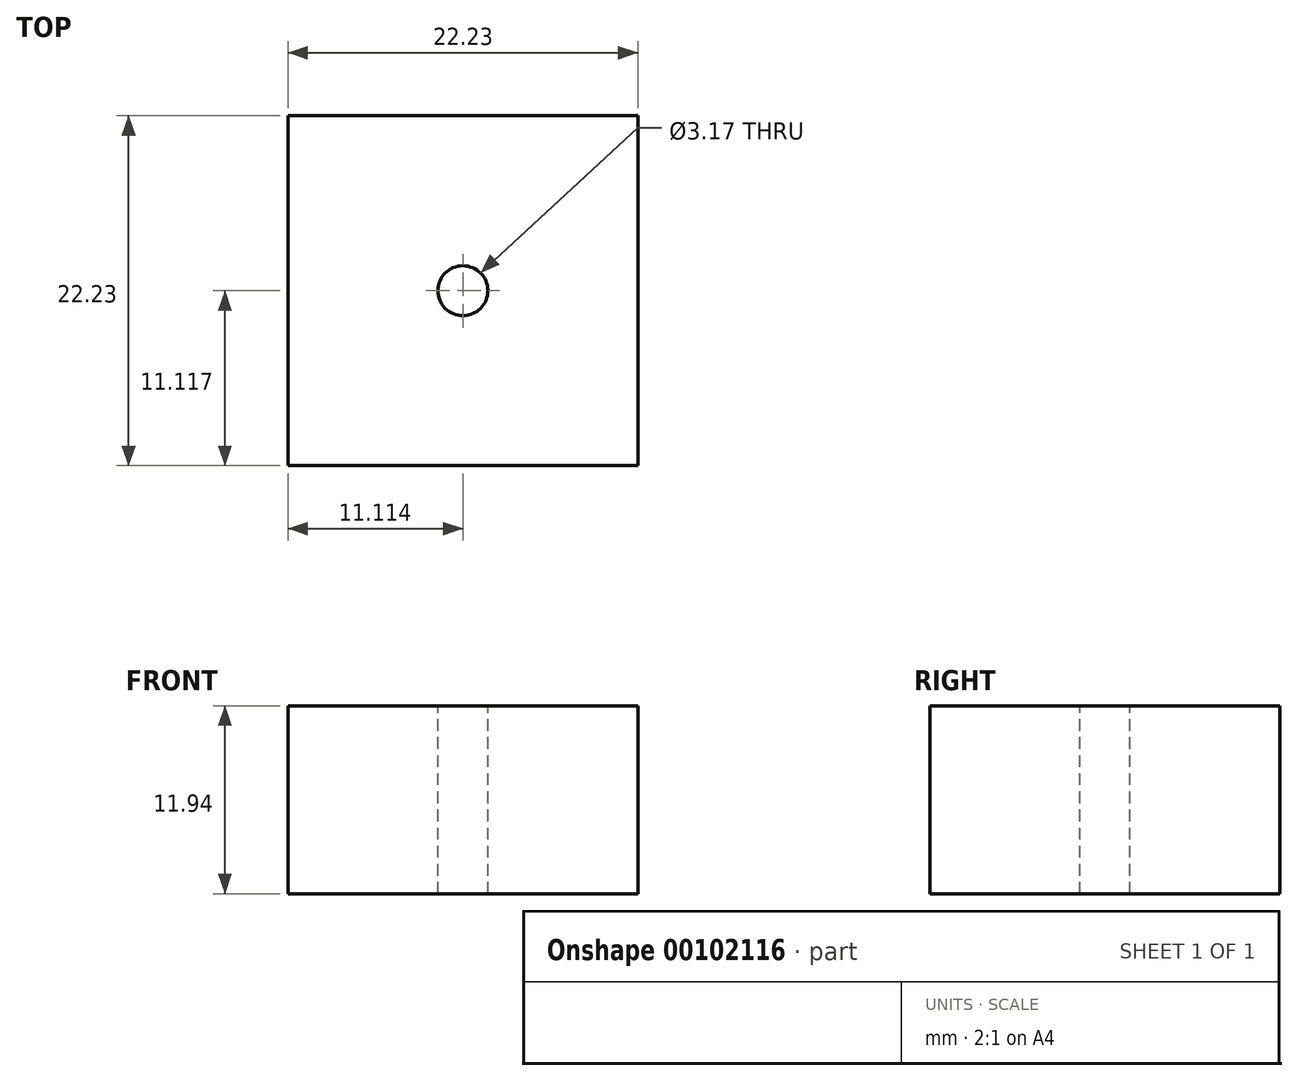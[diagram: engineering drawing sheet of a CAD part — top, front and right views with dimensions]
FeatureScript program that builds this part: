
annotation { "Feature Type Name" : "Feature", "Feature Type Description" : "" }
export const myFeature = defineFeature(function(context is Context, id is Id, definition is map)
    precondition{}
    {
        {
            var Q0;
            Q0=qCreatedBy(makeId("Top.planeOp"),FACE);
            var sketch = newSketch(context, id + "F0", { "sketchPlane" : qUnion([Q0])});
            skLineSegment(sketch, "E0.bottom", {"start": v(-1.19, 7.98) * mm, "end": v(21.04, 7.98) * mm});
            skLineSegment(sketch, "E0.top", {"start": v(-1.19, -14.25) * mm, "end": v(21.04, -14.25) * mm});
            skLineSegment(sketch, "E0.left", {"start": v(-1.19, 7.98) * mm, "end": v(-1.19, -14.25) * mm});
            skLineSegment(sketch, "E0.right", {"start": v(21.04, 7.98) * mm, "end": v(21.04, -14.25) * mm});
            skSolve(sketch);
        }
        {
            var Q0;
            Q0=makeQuery(id+"F0.imprint","IMPRINT",FACE,{"disambiguationData":[TD([[makeQuery(id+"F0.imprint","IMPRINT",EDGE,{"derivedFrom":sQuery(id+"F0.wireOp",EDGE,"E0.bottom")}),-1.0]])]});
            extrude(context, id + "F1", {"entities" : qUnion([Q0]), "depth" : 11.94 * mm});
        }
        {
            var Q0;
            Q0=makeQuery(id+"F1.opExtrude","CAP_FACE",FACE,{"disambiguationData":[OSD([sQuery(id+"F0.wireOp",EDGE,"E0.bottom"),sQuery(id+"F0.wireOp",EDGE,"E0.top"),sQuery(id+"F0.wireOp",EDGE,"E0.left"),sQuery(id+"F0.wireOp",EDGE,"E0.right")])],"isStart":false});
            var sketch = newSketch(context, id + "F2", { "sketchPlane" : qUnion([Q0])});
            skCircle(sketch, "E1", {"center": v(9.92, -3.13) * mm, "radius": 1.59 * mm});
            skPoint(sketch, "E1.centerSnap0", {"position": v(-1.19, -3.13) * mm});
            skPoint(sketch, "E1.centerSnap1", {"position": v(9.92, -14.25) * mm});
            skSolve(sketch);
        }
        {
            var Q0;
            Q0=makeQuery(id+"F2.imprint","IMPRINT",FACE,{"disambiguationData":[TD([[makeQuery(id+"F2.imprint","IMPRINT",EDGE,{"derivedFrom":sQuery(id+"F2.wireOp",EDGE,"E1")}),1.0]])]});
            extrude(context, id + "F3", {"entities" : qUnion([Q0]), "operationType" : NewBodyOperationType.REMOVE, "oppositeDirection" : true, "depth" : 25.4 * mm});
        }
    });
